# Revit family: LAMP_MINI SHOT BRACKET G2
name_source: partatom
category: Modelos genéricos
revit_build: Autodesk Revit 2015 (Build: 20140606_1530(x64)
units: mm (PartAtom-declared; Revit-internal decimal feet)

## types (24) — shared parameters
CRI = 80
Comentarios de tipo = Availability of tilting between -30º and 90º when placed in a project.
Elevación por defecto = 1219 mm
Fabricante = LAMP
Gear = Electronic
Height = 360 mm  [stored 1.1811 ft]
IEE = A+
Installation instructions = http://www.lamp.es
Insulation class = II
LED Lifetime = 60.000 L90 B10
Lamp = HIGH POWER LED
Last update = 11/04/2019
Luminaire type = Outdoor - Spotlight
MacAdam = 3
Manufacturer URL = http://www.lamp.es
Manufacturer country = Spain
Manufacturer name = LAMP
Model explanation = Availability of tilting between -30º and 90º when placed in a project.
Power Supply = 220-240V 50/60Hz
Product URL = http://www.lamp.es
Product datasheet = http://www.lamp.es
Protection rating = IP65 / IK06
Type = HI POWER NICHIA

## per-type parameters (varying)
| type | Descripción | Efficacy | Finish | Initial color | Initial intensity | Material cabeza | Material cuerpo | Modelo | Photometric web file | Plum | Power | Product code | Weight |
| 1097LM 3000 MEDIUM FLOOD ANT | MINI SHOT G2 BR 1500 WW MFL ANT. | 83 lm/W | Textured anthracite grey | 3000 K | 1097 lm | LAMP_Aluminio Shot Antracita | LAMP_Aluminio Shot Antracita | MN2BR15MF830NA | Cabeza MiniShot : 1097LM 3000 MEDIUM FLOOD | 13 W | 10 W | MN2BR15MF830NA | 2.79 kg |
| 1097LM 3000 MEDIUM FLOOD GR | MINI SHOT G2 BR 1500 WW MFL GR. | 83 lm/W | Texturised grey | 3000 K | 1097 lm | LAMP_Aluminio Shot | LAMP_Aluminio Shot | MN2BR15MF830NG | Cabeza MiniShot : 1097LM 3000 MEDIUM FLOOD | 13 W | 10 W | MN2BR15MF830NG | 2.79 kg |
| 1097LM 4000 MEDIUM FLOOD ANT | MINI SHOT G2 BR 1500 NW MFL ANT. | 83 lm/W | Textured anthracite grey | 4000 K | 1097 lm | LAMP_Aluminio Shot Antracita | LAMP_Aluminio Shot Antracita | MN2BR15MF840NA | Cabeza MiniShot : 1097LM 4000 MEDIUM FLOOD | 13 W | 10 W | MN2BR15MF840NA | 2.79 kg |
| 1097LM 4000 MEDIUM FLOOD GR | MINI SHOT G2 BR 1500 NW MFL GR. | 83 lm/W | Texturised grey | 4000 K | 1097 lm | LAMP_Aluminio Shot | LAMP_Aluminio Shot | MN2BR15MF840NG | Cabeza MiniShot : 1097LM 4000 MEDIUM FLOOD | 13 W | 10 W | MN2BR15MF840NG | 2.79 kg |
| 1146LM 3000 SPOT ANT | MINI SHOT G2 BR 1500 WW SP ANT. | 87 lm/W | Textured anthracite grey | 3000 K | 1146 lm | LAMP_Aluminio Shot Antracita | LAMP_Aluminio Shot Antracita | MN2BR15SP830NA | Cabeza MiniShot : 1146LM 3000 SPOT | 13 W | 10 W | MN2BR15SP830NA | 2.79 kg |
| 1146LM 3000 SPOT GR | MINI SHOT G2 BR 1500 WW SP GR. | 87 lm/W | Texturised grey | 3000 K | 1146 lm | LAMP_Aluminio Shot | LAMP_Aluminio Shot | MN2BR15SP830NG | Cabeza MiniShot : 1146LM 3000 SPOT | 13 W | 10 W | MN2BR15SP830NG | 2.79 kg |
| 1146LM 4000 SPOT ANT | MINI SHOT G2 BR 1500 NW SP ANT. | 87 lm/W | Textured anthracite grey | 4000 K | 1146 lm | LAMP_Aluminio Shot Antracita | LAMP_Aluminio Shot Antracita | MN2BR15SP840NA | Cabeza MiniShot : 1146LM 4000 SPOT | 13 W | 10 W | MN2BR15SP840NA | 2.79 kg |
| 1146LM 4000 SPOT GR | MINI SHOT G2 BR 1500 NW SP GR. | 87 lm/W | Texturised grey | 4000 K | 1146 lm | LAMP_Aluminio Shot | LAMP_Aluminio Shot | MN2BR15SP840NG | Cabeza MiniShot : 1146LM 4000 SPOT | 13 W | 10 W | MN2BR15SP840NG | 2.79 kg |
| 2155LM 3000 MEDIUM FLOOD ANT | MINI SHOT G2 BR 2900 WW MFL ANT. | 94 lm/W | Textured anthracite grey | 3000 K | 2155 lm | LAMP_Aluminio Shot Antracita | LAMP_Aluminio Shot Antracita | MN2BR30MF830NA | Cabeza MiniShot : 2155LM 3000 MEDIUM FLOOD | 23 W | 20 W | MN2BR30MF830NA | 2.82 kg |
| 2155LM 3000 MEDIUM FLOOD GR | MINI SHOT G2 BR 2900 WW MFL GR. | 94 lm/W | Texturised grey | 3000 K | 2155 lm | LAMP_Aluminio Shot | LAMP_Aluminio Shot | MN2BR30MF830NG | Cabeza MiniShot : 2155LM 3000 MEDIUM FLOOD | 23 W | 20 W | MN2BR30MF830NG | 2.82 kg |
| 2155LM 4000 MEDIUM FLOOD ANT | MINI SHOT G2 BR 2900 NW MFL ANT. | 94 lm/W | Textured anthracite grey | 4000 K | 2155 lm | LAMP_Aluminio Shot Antracita | LAMP_Aluminio Shot Antracita | MN2BR30MF840NA | Cabeza MiniShot : 2155LM 4000 MEDIUM FLOOD | 23 W | 20 W | MN2BR30MF840NA | 2.82 kg |
| 2155LM 4000 MEDIUM FLOOD GR | MINI SHOT G2 BR 2900 NW MFL GR. | 94 lm/W | Texturised grey | 4000 K | 2155 lm | LAMP_Aluminio Shot | LAMP_Aluminio Shot | MN2BR30MF840NG | Cabeza MiniShot : 2155LM 4000 MEDIUM FLOOD | 23 W | 20 W | MN2BR30MF840NG | 2.82 kg |
| 2215LM 3000 SPOT ANT | MINI SHOT G2 BR 2900 WW SP ANT. | 96 lm/W | Textured anthracite grey | 3000 K | 2215 lm | LAMP_Aluminio Shot Antracita | LAMP_Aluminio Shot Antracita | MN2BR30SP830NA | Cabeza MiniShot : 2215LM 3000 SPOT | 23 W | 20 W | MN2BR30SP830NA | 2.82 kg |
| 2215LM 3000 SPOT GR | MINI SHOT G2 BR 2900 WW SP GR. | 96 lm/W | Texturised grey | 3000 K | 2215 lm | LAMP_Aluminio Shot | LAMP_Aluminio Shot | MN2BR30SP830NG | Cabeza MiniShot : 2215LM 3000 SPOT | 23 W | 20 W | MN2BR30SP830NG | 2.82 kg |
| 2215LM 4000 SPOT ANT | MINI SHOT G2 BR 2900 NW SP ANT. | 96 lm/W | Textured anthracite grey | 4000 K | 2215 lm | LAMP_Aluminio Shot Antracita | LAMP_Aluminio Shot Antracita | MN2BR30SP840NA | Cabeza MiniShot : 2215LM 4000 SPOT | 23 W | 20 W | MN2BR30SP840NA | 2.82 kg |
| 2215LM 4000 SPOT GR | MINI SHOT G2 BR 2900 NW SP GR. | 96 lm/W | Texturised grey | 4000 K | 2215 lm | LAMP_Aluminio Shot | LAMP_Aluminio Shot | MN2BR30SP840NG | Cabeza MiniShot : 2215LM 4000 SPOT | 23 W | 20 W | MN2BR30SP840NG | 2.82 kg |
| 2937LM 3000 MEDIUM FLOOD ANT | MINI SHOT G2 BR 3800 WW MFL ANT. | 88 lm/W | Textured anthracite grey | 3000 K | 2937 lm | LAMP_Aluminio Shot Antracita | LAMP_Aluminio Shot Antracita | MN2BR40MF830NA | Cabeza MiniShot : 2937LM 3000 MEDIUM FLOOD | 34 W | 30 W | MN2BR40MF830NA | 2.82 kg |
| 2937LM 3000 MEDIUM FLOOD GR | MINI SHOT G2 BR 3800 WW MFL GR. | 88 lm/W | Texturised grey | 3000 K | 2937 lm | LAMP_Aluminio Shot | LAMP_Aluminio Shot | MN2BR40MF830NG | Cabeza MiniShot : 2937LM 3000 MEDIUM FLOOD | 34 W | 30 W | MN2BR40MF830NG | 2.82 kg |
| 2937LM 4000 MEDIUM FLOOD ANT | MINI SHOT G2 BR 3800 NW MFL ANT. | 88 lm/W | Textured anthracite grey | 4000 K | 2937 lm | LAMP_Aluminio Shot Antracita | LAMP_Aluminio Shot Antracita | MN2BR40MF840NA | Cabeza MiniShot : 2937LM 4000 MEDIUM FLOOD | 34 W | 30 W | MN2BR40MF840NA | 2.82 kg |
| 2937LM 4000 MEDIUM FLOOD GR | MINI SHOT G2 BR 3800 NW MFL GR. | 88 lm/W | Texturised grey | 4000 K | 2937 lm | LAMP_Aluminio Shot | LAMP_Aluminio Shot | MN2BR40MF840NG | Cabeza MiniShot : 2937LM 4000 MEDIUM FLOOD | 34 W | 30 W | MN2BR40MF840NG | 2.82 kg |
| 3032LM 3000 SPOT ANT | MINI SHOT G2 BR 3800 WW SP ANT. | 91 lm/W | Textured anthracite grey | 3000 K | 3032 lm | LAMP_Aluminio Shot Antracita | LAMP_Aluminio Shot Antracita | MN2BR40SP830NA | Cabeza MiniShot : 3032LM 3000 SPOT | 34 W | 30 W | MN2BR40SP830NA | 2.82 kg |
| 3032LM 3000 SPOT GR | MINI SHOT G2 BR 3800 WW SP GR. | 91 lm/W | Texturised grey | 3000 K | 3032 lm | LAMP_Aluminio Shot | LAMP_Aluminio Shot | MN2BR40SP830NG | Cabeza MiniShot : 3032LM 3000 SPOT | 34 W | 30 W | MN2BR40SP830NG | 2.82 kg |
| 3032LM 4000 SPOT ANT | MINI SHOT G2 BR 3800 NW SP ANT. | 91 lm/W | Textured anthracite grey | 4000 K | 3032 lm | LAMP_Aluminio Shot Antracita | LAMP_Aluminio Shot Antracita | MN2BR40SP840NA | Cabeza MiniShot : 3032LM 4000 SPOT | 34 W | 30 W | MN2BR40SP840NA | 2.82 kg |
| 3032LM 4000 SPOT GR | MINI SHOT G2 BR 3800 NW SP GR. | 91 lm/W | Texturised grey | 4000 K | 3032 lm | LAMP_Aluminio Shot | LAMP_Aluminio Shot | MN2BR40SP840NG | Cabeza MiniShot : 3032LM 4000 SPOT | 34 W | 30 W | MN2BR40SP840NG | 2.82 kg |

note: [stored X ft] marks values corroborated as IEEE doubles in the binary element streams (Revit-internal decimal feet)
